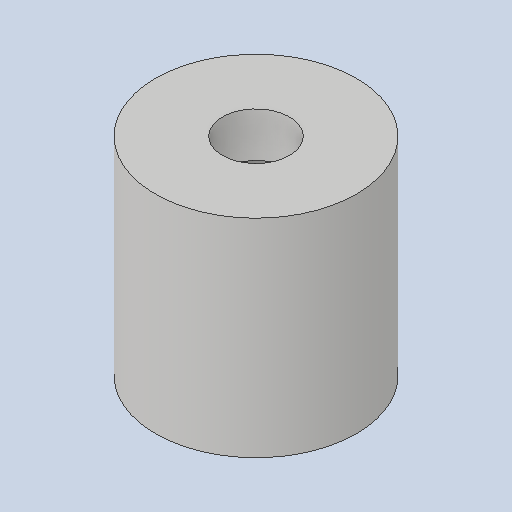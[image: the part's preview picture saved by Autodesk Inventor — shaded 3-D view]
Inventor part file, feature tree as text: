
AUTODESK INVENTOR PART (.ipt)
format: ipt  version: 2023 (Build 270158000, 158)  size: 125,952 bytes
history: native  units: mm
features: sketch x4, extrude x3, projected_geometry x2
ambient origin geometry x8: Origin, YZ Plane, XZ Plane, XY Plane, X Axis, Y Axis, Z Axis, Center Point
bodies: Solid1 (feature_tree)
feature tree (9):
  extrude  "Extrusion1"  Depth=9.0mm
  extrude  "Extrusion2"  Depth=3.3mm TaperAngle=0.0deg
  sketch  "Sketch3"  dims[d5=3.0mm d6=2.0mm d7=0.0mm]
  extrude  "Extrusion3"  Depth=2.0mm TaperAngle=0.0deg
  sketch  "Sketch1"  dims[d0=3.0mm d1=9.0mm]
  sketch  "Sketch2"  dims[d2=5.55mm d3=3.3mm d4=0.0mm]
  projected_geometry  "Projected Loop1"
  sketch  "Sketch4"  dims[d8=6.1mm d9=4.0mm d10=0.0mm]
  projected_geometry  "Projected Loop2"
